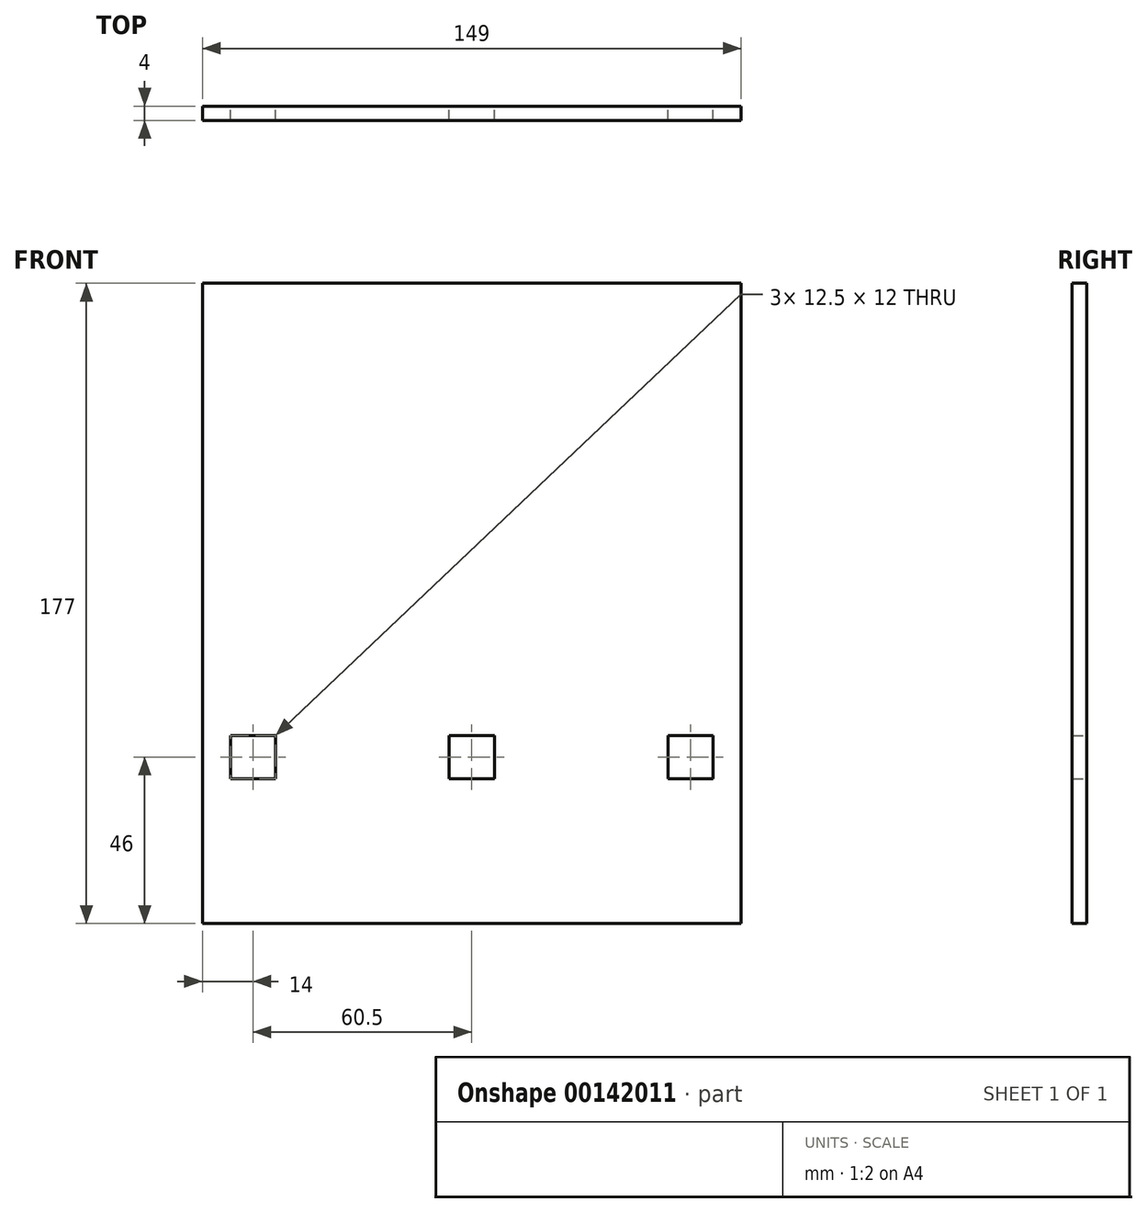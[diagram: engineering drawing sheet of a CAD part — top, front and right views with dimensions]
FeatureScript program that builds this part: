
annotation { "Feature Type Name" : "Feature", "Feature Type Description" : "" }
export const myFeature = defineFeature(function(context is Context, id is Id, definition is map)
    precondition{}
    {
        {
            var Q0;
            Q0=qCreatedBy(makeId("Front.planeOp"),FACE);
            var sketch = newSketch(context, id + "F0", { "sketchPlane" : qUnion([Q0])});
            skLineSegment(sketch, "E0.bottom", {"start": v(74.5, 88.5) * mm, "end": v(-74.5, 88.5) * mm});
            skLineSegment(sketch, "E0.top", {"start": v(74.5, -88.5) * mm, "end": v(-74.5, -88.5) * mm});
            skLineSegment(sketch, "E0.left", {"start": v(74.5, 88.5) * mm, "end": v(74.5, -88.5) * mm});
            skLineSegment(sketch, "E0.right", {"start": v(-74.5, 88.5) * mm, "end": v(-74.5, -88.5) * mm});
            skPoint(sketch, "E0.middle", {"position": v(0, 0) * mm});
            skLineSegment(sketch, "E1", {"start": v(-74.5, -36.5) * mm, "end": v(74.5, -36.5) * mm, "construction": true});
            skLineSegment(sketch, "E2.bottom", {"start": v(6.25, -36.5) * mm, "end": v(-6.25, -36.5) * mm});
            skLineSegment(sketch, "E2.top", {"start": v(6.25, -48.5) * mm, "end": v(-6.25, -48.5) * mm});
            skLineSegment(sketch, "E2.left", {"start": v(6.25, -36.5) * mm, "end": v(6.25, -48.5) * mm});
            skLineSegment(sketch, "E2.right", {"start": v(-6.25, -36.5) * mm, "end": v(-6.25, -48.5) * mm});
            skLineSegment(sketch, "E3.bottom", {"start": v(-66.75, -36.5) * mm, "end": v(-54.25, -36.5) * mm});
            skLineSegment(sketch, "E3.top", {"start": v(-66.75, -48.5) * mm, "end": v(-54.25, -48.5) * mm});
            skLineSegment(sketch, "E3.left", {"start": v(-66.75, -36.5) * mm, "end": v(-66.75, -48.5) * mm});
            skLineSegment(sketch, "E3.right", {"start": v(-54.25, -36.5) * mm, "end": v(-54.25, -48.5) * mm});
            skLineSegment(sketch, "E4.bottom", {"start": v(54.25, -36.5) * mm, "end": v(66.75, -36.5) * mm});
            skLineSegment(sketch, "E4.top", {"start": v(54.25, -48.5) * mm, "end": v(66.75, -48.5) * mm});
            skLineSegment(sketch, "E4.left", {"start": v(54.25, -36.5) * mm, "end": v(54.25, -48.5) * mm});
            skLineSegment(sketch, "E4.right", {"start": v(66.75, -36.5) * mm, "end": v(66.75, -48.5) * mm});
            skPoint(sketch, "E5", {"position": v(0, -48.5) * mm});
            skLineSegment(sketch, "E6", {"start": v(0, 88.5) * mm, "end": v(0, -88.5) * mm, "construction": true});
            skLineSegment(sketch, "E7", {"start": v(-74.5, 68.5) * mm, "end": v(74.5, 68.5) * mm, "construction": true});
            skSolve(sketch);
        }
        {
            var Q0;
            Q0=makeQuery(id+"F0.imprint","IMPRINT",FACE,{"disambiguationData":[TD([[makeQuery(id+"F0.imprint","IMPRINT",EDGE,{"derivedFrom":sQuery(id+"F0.wireOp",EDGE,"E0.bottom")}),1.0]])]});
            extrude(context, id + "F1", {"entities" : qUnion([Q0]), "depth" : 2 * mm, "hasSecondDirection" : true, "secondDirectionOppositeDirection" : true, "secondDirectionDepth" : 2 * mm});
        }
    });
